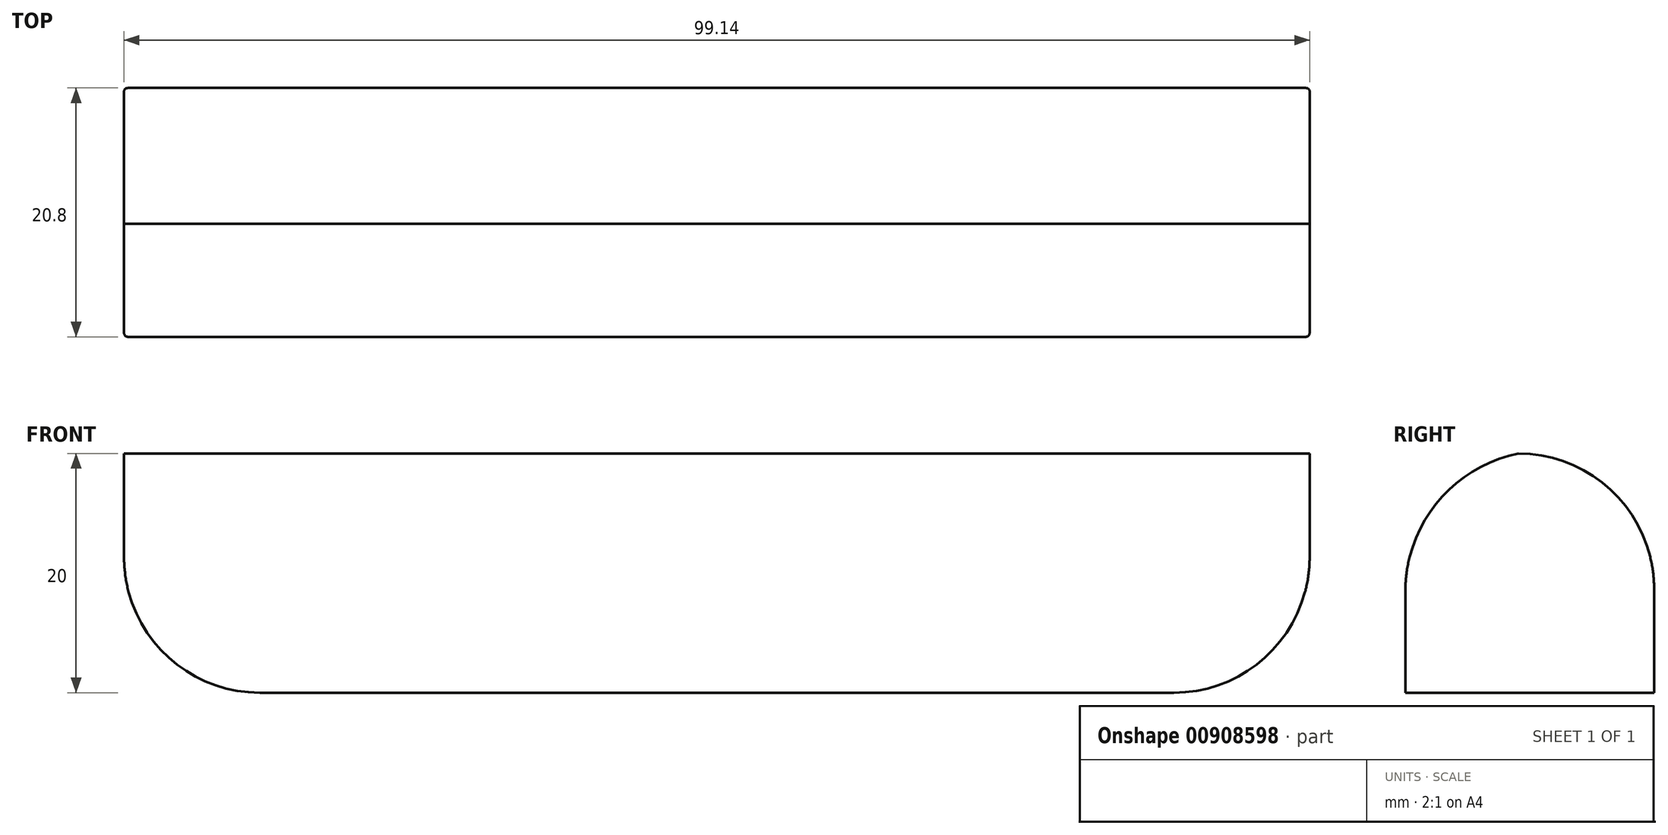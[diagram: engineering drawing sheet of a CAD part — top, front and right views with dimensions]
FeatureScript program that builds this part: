
annotation { "Feature Type Name" : "Feature", "Feature Type Description" : "" }
export const myFeature = defineFeature(function(context is Context, id is Id, definition is map)
    precondition{}
    {
        {
            var Q0;
            Q0=qCreatedBy(makeId("Top.planeOp"),FACE);
            var sketch = newSketch(context, id + "F0", { "sketchPlane" : qUnion([Q0])});
            skLineSegment(sketch, "E0.bottom", {"start": v(0, 0) * mm, "end": v(-49.57, 0) * mm});
            skLineSegment(sketch, "E0.top", {"start": v(0, -20.8) * mm, "end": v(-49.57, -20.8) * mm});
            skLineSegment(sketch, "E0.left", {"start": v(0, 0) * mm, "end": v(0, -20.8) * mm});
            skLineSegment(sketch, "E0.right", {"start": v(-49.57, 0) * mm, "end": v(-49.57, -20.8) * mm});
            skSolve(sketch);
        }
        {
            var Q0;
            Q0=makeQuery(id+"F0.imprint","IMPRINT",FACE,{"disambiguationData":[TD([[makeQuery(id+"F0.imprint","IMPRINT",EDGE,{"derivedFrom":sQuery(id+"F0.wireOp",EDGE,"E0.bottom")}),1.0]])]});
            extrude(context, id + "F1", {"entities" : qUnion([Q0]), "depth" : 20 * mm, "offsetDistance" : 25 * mm});
        }
        {
            var Q0;
            Q0=makeQuery(id+"F1.opExtrude","CAP_EDGE",EDGE,{"disambiguationData":[OSD([sQuery(id+"F0.wireOp",EDGE,"E0.bottom")])],"isStart":false});
            fillet(context, id + "F2", {"entities" : qUnion([Q0]), "radius" : 11.35 * mm, "tangentPropagation" : true, "allowEdgeOverflow" : false});
        }
        {
            var Q0;
            Q0=makeQuery(id+"F1.opExtrude","CAP_EDGE",EDGE,{"disambiguationData":[OSD([sQuery(id+"F0.wireOp",EDGE,"E0.top")])],"isStart":false});
            fillet(context, id + "F3", {"entities" : qUnion([Q0]), "radius" : 11.83 * mm, "tangentPropagation" : true, "allowEdgeOverflow" : false});
        }
        {
            var Q0;
            Q0=makeQuery(id+"F1.opExtrude","CAP_EDGE",EDGE,{"disambiguationData":[OSD([sQuery(id+"F0.wireOp",EDGE,"E0.right")])],"isStart":true});
            fillet(context, id + "F4", {"entities" : qUnion([Q0]), "radius" : 11.35 * mm, "tangentPropagation" : true, "allowEdgeOverflow" : false});
        }
        {
            var Q0;
            Q0=makeQuery(id+"F1.opExtrude","SWEPT_BODY",BODY,{"disambiguationData":[OSD([sQuery(id+"F0.wireOp",EDGE,"E0.bottom"),sQuery(id+"F0.wireOp",EDGE,"E0.top"),sQuery(id+"F0.wireOp",EDGE,"E0.left"),sQuery(id+"F0.wireOp",EDGE,"E0.right")])]});
            var Q1;
            Q1=makeQuery(id+"F1.opExtrude","SWEPT_FACE",FACE,{"disambiguationData":[OSD([sQuery(id+"F0.wireOp",EDGE,"E0.left")])]});
            mirror(context, id + "F5", {"operationType" : NewBodyOperationType.ADD, "entities" : qUnion([Q0]), "mirrorPlane" : qUnion([Q1])});
        }
    });
